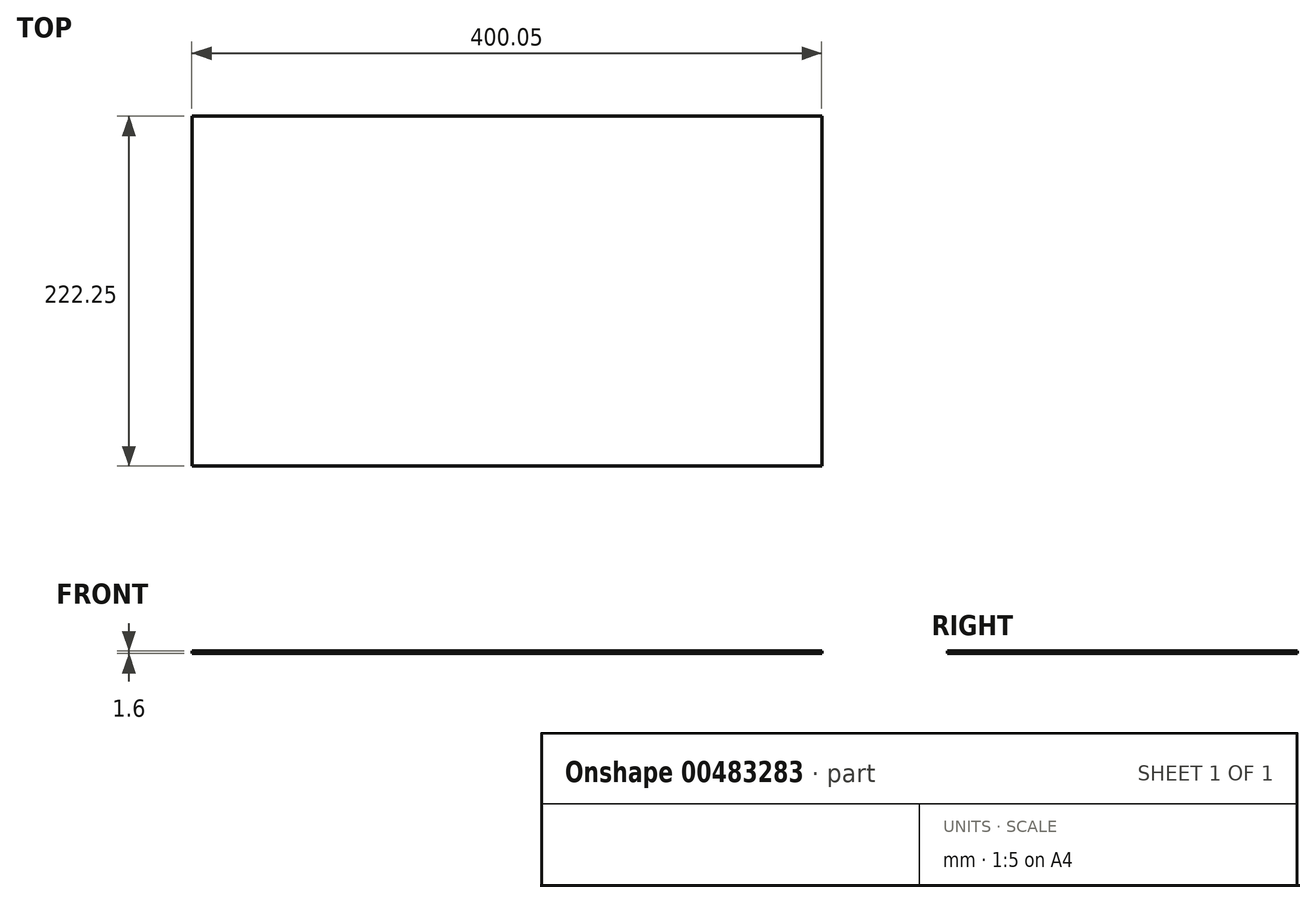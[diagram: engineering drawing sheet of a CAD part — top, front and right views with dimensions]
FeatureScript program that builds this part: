
annotation { "Feature Type Name" : "Feature", "Feature Type Description" : "" }
export const myFeature = defineFeature(function(context is Context, id is Id, definition is map)
    precondition{}
    {
        {
            var Q0;
            Q0=qCreatedBy(makeId("Top.planeOp"),FACE);
            var sketch = newSketch(context, id + "F0", { "sketchPlane" : qUnion([Q0])});
            skLineSegment(sketch, "E0.bottom", {"start": v(-216.7, 107.19) * mm, "end": v(183.35, 107.19) * mm});
            skLineSegment(sketch, "E0.top", {"start": v(-216.7, -115.06) * mm, "end": v(183.35, -115.06) * mm});
            skLineSegment(sketch, "E0.left", {"start": v(-216.7, 107.19) * mm, "end": v(-216.7, -115.06) * mm});
            skLineSegment(sketch, "E0.right", {"start": v(183.35, 107.19) * mm, "end": v(183.35, -115.06) * mm});
            skSolve(sketch);
        }
        {
            var Q0;
            Q0 = qSketchRegion(id + "F0", true);
            extrude(context, id + "F1", {"entities" : qUnion([Q0]), "depth" : 1.6 * mm});
        }
    });
